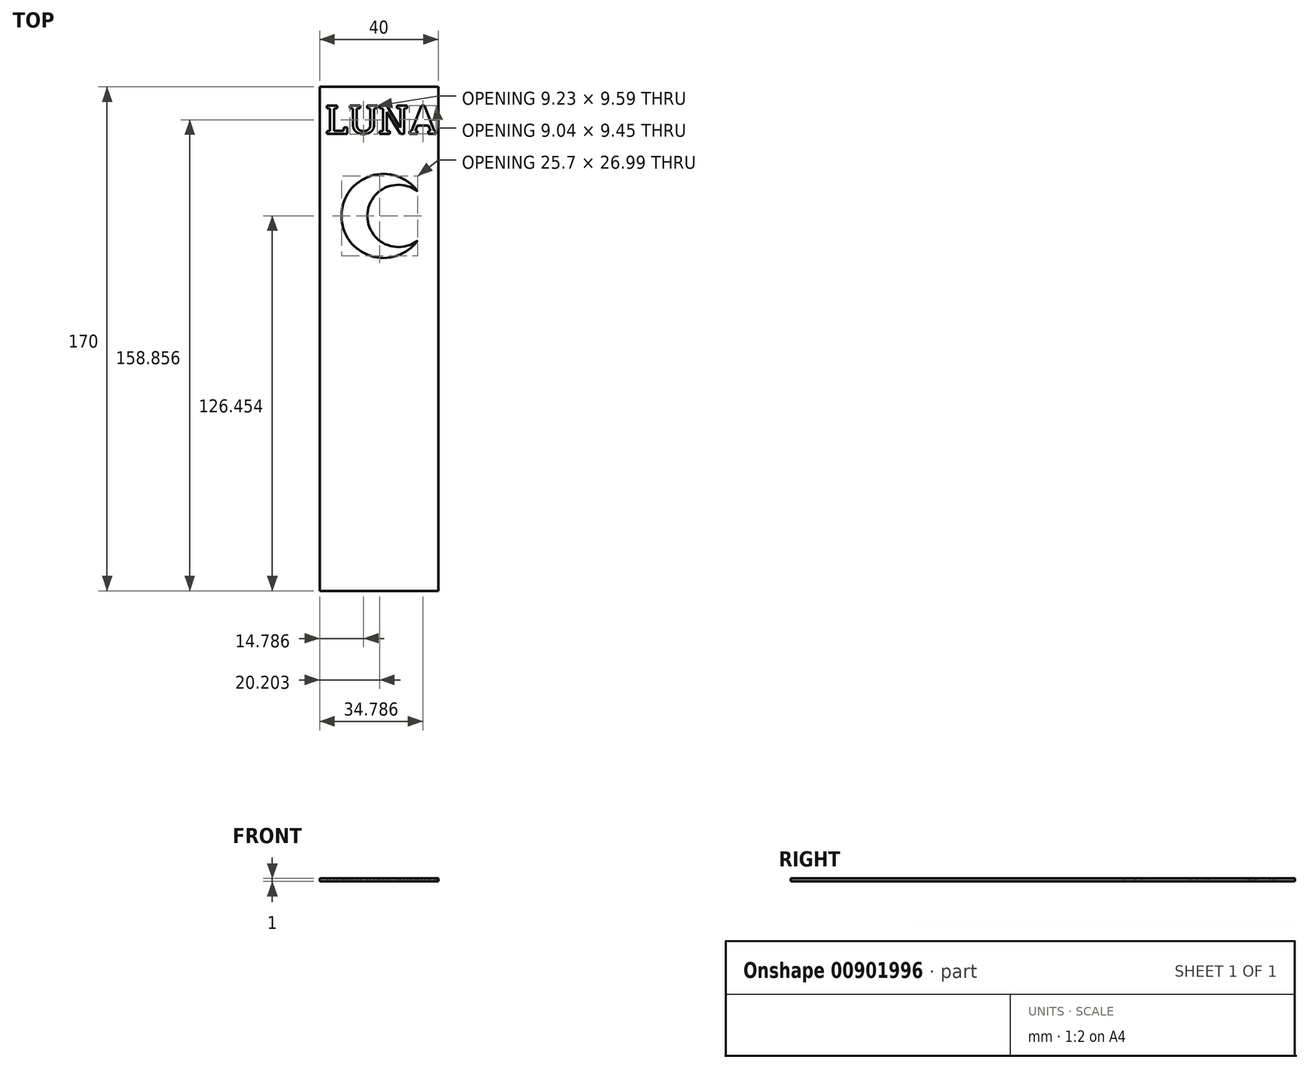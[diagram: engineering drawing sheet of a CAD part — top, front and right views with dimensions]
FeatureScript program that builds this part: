
annotation { "Feature Type Name" : "Feature", "Feature Type Description" : "" }
export const myFeature = defineFeature(function(context is Context, id is Id, definition is map)
    precondition{}
    {
        {
            var Q0;
            Q0=qCreatedBy(makeId("Top.planeOp"),FACE);
            var sketch = newSketch(context, id + "F0", { "sketchPlane" : qUnion([Q0])});
            skLineSegment(sketch, "E0.bottom", {"start": v(-21.52, 100.34) * mm, "end": v(18.48, 100.34) * mm});
            skLineSegment(sketch, "E0.top", {"start": v(-21.52, -69.66) * mm, "end": v(18.48, -69.66) * mm});
            skLineSegment(sketch, "E0.left", {"start": v(-21.52, 100.34) * mm, "end": v(-21.52, -69.66) * mm});
            skLineSegment(sketch, "E0.right", {"start": v(18.48, 100.34) * mm, "end": v(18.48, -69.66) * mm});
            skText(sketch, "E1", { "text": "LUNA\n", "fontName": "RobotoSlab-Regular.ttf"});
            skArc(sketch, "E2", {"start": v(11.53, 65.02) * mm, "mid": v(-14.17, 56.8) * mm, "end": v(11.53, 48.57) * mm});
            skArc(sketch, "E3", {"start": v(11.53, 65.02) * mm, "mid": v(-5.46, 56.8) * mm, "end": v(11.53, 48.57) * mm});
            const initialGuessF0  = {"E1": [-0.01952, 0.08454, 1, 0, 0.00957]};
            skSetInitialGuess(sketch, initialGuessF0);
            skSolve(sketch);
        }
        {
            var Q0;
            Q0 = qSketchRegion(id + "F0", true);
            extrude(context, id + "F1", {"entities" : qUnion([Q0]), "depth" : 1 * mm, "offsetDistance" : 25 * mm});
        }
    });
